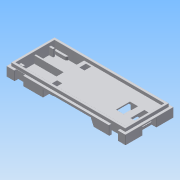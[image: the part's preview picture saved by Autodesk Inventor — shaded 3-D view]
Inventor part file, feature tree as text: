
AUTODESK INVENTOR PART (.ipt)
format: ipt  version: 2015 SP1 (Build 190203100, 203)  size: 712,704 bytes
history: native  units: mm
features: extrude x19, sketch x19, fillet x13, other x4, mirror x3, projected_geometry x2
ambient origin geometry x8: Origin, YZ Plane, XZ Plane, XY Plane, X Axis, Y Axis, Z Axis, Center Point
bodies: Body1 (feature_tree)
feature tree (60):
  other  "Твердое тело1"
  extrude  "Выдавливание1"  Depth=90.2mm
  extrude  "Выдавливание2"  Depth=36.3mm
  extrude  "Выдавливание3"  Depth=2.0mm TaperAngle=0.0deg
  extrude  "Выдавливание4"  Depth=1.85mm
  extrude  "Выдавливание5"  Depth=1.85mm
  extrude  "Выдавливание6"  Depth=1.7mm
  extrude  "Выдавливание7"  Depth=1.7mm
  extrude  "Выдавливание8"  Depth=1.7mm
  extrude  "Выдавливание9"  Depth=1.7mm
  extrude  "Выдавливание10"  Depth=1.7mm
  fillet  "Сопряжение1"  Radius=1.7mm
  extrude  "Выдавливание11"  Depth=2.4mm TaperAngle=0.0deg
  mirror  "Зеркальное отражение1"
  extrude  "Выдавливание12"  Depth=10.5mm
  extrude  "Выдавливание13"  Depth=38.0mm
  other  "РабПлоскость1"
  extrude  "Выдавливание14"  Depth=1.1mm TaperAngle=0.0deg
  other  "РабПлоскость2"
  extrude  "Выдавливание15"  Depth=27.7mm
  extrude  "Выдавливание16"  Depth=5.1mm TaperAngle=0.0deg
  mirror  "Зеркальное отражение3"
  extrude  "Выдавливание17"  Depth=6.5mm
  extrude  "Выдавливание19"  Depth=1.5mm
  extrude  "Выдавливание20"  Depth=6.5mm
  fillet  "Сопряжение2"  Radius=1.5mm
  mirror  "Зеркальное отражение4"
  fillet  "Сопряжение3"  Radius=6.0mm
  fillet  "Сопряжение4"  Radius=6.0mm
  fillet  "Сопряжение5"  Radius=7.1mm
  fillet  "Сопряжение6"  Radius=1.5mm
  fillet  "Сопряжение7"  Radius=1.5mm
  fillet  "Сопряжение8"  Radius=3.0mm
  fillet  "Сопряжение9"  Radius=36.0mm
  fillet  "Сопряжение10"  Radius=38.2mm
  fillet  "Сопряжение11"  Radius=5.1mm
  fillet  "Сопряжение12"  Radius=6.0mm
  fillet  "Сопряжение13"  Radius=6.5mm
  sketch  "Эскиз1"
  sketch  "Эскиз2"
  sketch  "Эскиз3"
  sketch  "Эскиз4"
  sketch  "Эскиз5"
  sketch  "Эскиз6"
  sketch  "Эскиз8"
  sketch  "Эскиз9"
  sketch  "Эскиз10"
  sketch  "Эскиз11"
  sketch  "Эскиз12"
  sketch  "Эскиз15"
  sketch  "Эскиз16"
  projected_geometry  "Спроецированная петля1"
  sketch  "Эскиз17"
  sketch  "Эскиз18"
  sketch  "Эскиз19"
  other  "РабПлоскость4"
  sketch  "Эскиз20"
  sketch  "Эскиз21"
  projected_geometry  "Спроецированная петля2"
  sketch  "Эскиз22"
